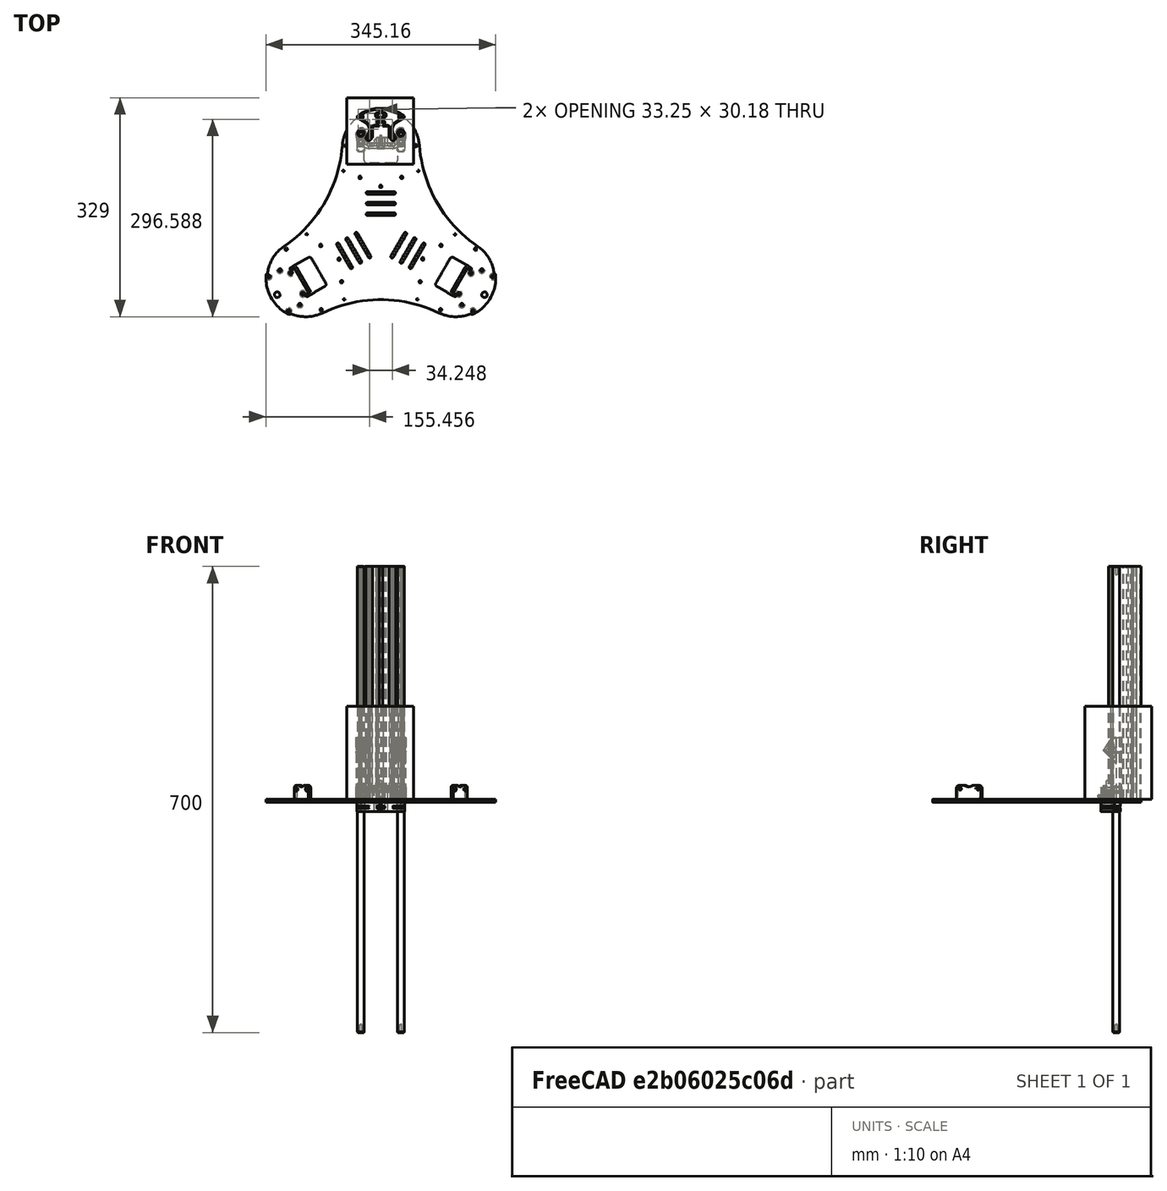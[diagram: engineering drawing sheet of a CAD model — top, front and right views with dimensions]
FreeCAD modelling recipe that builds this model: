
FCSTD DOCUMENT  (FreeCAD 0.18R16146 (Git))
Label: Vertical-Slider_w_FlyingExtruder
License: All rights reserved
LicenseURL: http://en.wikipedia.org/wiki/All_rights_reserved
objects: Part::FeaturePython×10, Part::Feature×9, Sketcher::SketchObject×6, App::Part×5, Part::Compound×3, PartDesign::Plane×3, PartDesign::Body×3, Spreadsheet::Sheet×2, PartDesign::Pocket×2, PartDesign::Hole×2, PartDesign::Revolution×1, Part::Box×1, App::DocumentObjectGroup×1, PartDesign::Point×1, PartDesign::AdditiveLoft×1, Part::Mirroring×1, PartDesign::FeatureBase×1, Part::MultiFuse×1
note: 51 computed .brp shape members not serialized (recipe doc carries the construction recipe); baked Part::Feature solids carry a one-line shape summary decoded from their .brp

FEATURE [Part::Feature] K8800_BAP
  Placement = pos=(0,-153,-2) rot=(0,0,1;0rad)
  shape: bbox 351.2 x 331.3 x 25.02 mm, 225 faces (baked)
FEATURE [Part::Feature] K8800_RD10  label="K8800_RodLeft"
  Placement = pos=(-30,0,0) rot=(0,0,1;0rad)
  shape: bbox 10 x 10 x 700 mm, 9 faces (baked)
FEATURE [Part::Feature] K8800_RD011  label="K8800_RodRight"
  Placement = pos=(30,0,0) rot=(0,0,1;0rad)
  shape: bbox 10 x 10 x 700 mm, 9 faces (baked)
FEATURE [Part::Feature] K8800_RI
  shape: bbox 70.64 x 62.27 x 700 mm, 164 faces (baked)
FEATURE [Part::Feature] K8800_VS
  Placement = pos=(0,0,0) rot=(0,0,1;1.5708rad)
  shape: bbox 72.01 x 24.93 x 46.6 mm, 535 faces (baked)
FEATURE [Part::Feature] K8800_LB10  label="K8800_LB10-L"
  Placement = pos=(-30,0,0) rot=(0,0,1;0rad)
  shape: bbox 12 x 12 x 36 mm, 16 faces (baked)
FEATURE [Part::Feature] K8800_LB10001  label="K8800_LB10-R"
  Placement = pos=(30,0,0) rot=(0,0,1;0rad)
  shape: bbox 12 x 12 x 36 mm, 16 faces (baked)
FEATURE [Spreadsheet::Sheet] Spreadsheet  label="Schrauben"
  cells = A1(M5RadiusBore)==2.5mm; B1=M5RadiusBore; C1=Radius der Bohrungen für M5-Schrauben; A2(M5HexNutWidth)==8mm; B2=M5HexNutWidth; C2=Schlüsselweite der M5-Muttern; A3(M5HexNutHeight)==4mm; B3=M5HexNutHeight; C3=Höhe der M5-Muttern; A4(M5HexHeadRadius)==4.7mm; B4=M5HexHeadRadius; C4=Radius des Schraubenkopfes; A5(M5HexHeadHeight)==5.1mm; B5=M5HexHeadHeight; C5=Höhe des Schraubenkopfes; A6(M5InsertHeight)==6mm; B6=M5InsertHeight; C6=Höhe des Insert; A7(M5InserWidth)==6.3mm; B7=M5InserWidth; C7=Durchmesser (Taille) des Insert; A8(MCThreadLength)==8.25mm; B8=MCThreadLength; C8=Gewindelänge der Magnetic Cups; A9(MCHeadHeight)==4.8mm; B9=MCHeadHeight; C9=Kopfhöhe der Magentic Cups; A10(MCHeadRadius)==8.5mm / 2; B10=MCHeadRadius; C10=Radius des Magnetic Cups
FEATURE [Spreadsheet::Sheet] Spreadsheet001  label="Global"
  cells = A1===========; B1=3D Druckparameter; C1===================================; A2(NozzleSize)==0.6mm; B2=NozzleSize; C2=Düsendurchmesser; A3(ExtMult)=0.9; B3=ExtMult; C3=Extrusion Multiplier; A4(NozzleWidth)==NozzleSize * ExtMult; B4=NozzeWidth; C4=Extrusion width; A5(numPerimeter)=3; B5=numPerimeter; C5=Anzahl der Perimeter; A6(Flesh)==2 * NozzleWidth; B6=Flesh; C6=Zusätzlicher Material; A7===========; B7=Bronzelager; C7===================================; A8(bearingID)==10mm; B8=bearingID; C8=Innendurchmesser Lager; A9(bearingOD)==13mm; B9=bearingOD; C9=Außendurchmesser Lager; A10(bearingLen)==20mm; B10=bearingLen; C10=Länge des Lagers; A11===========; B11=Mechanik Lager; C11===================================; A12(distRods)==60mm; B12=distRods; C12=Abstand der Wellen; A13(diaRods)==10mm; B13=diaRods; C13=Durchmesser der Wellen; A14(clearanceRods)==NozzleWidth / 2; B14=clearanceRods; C14=Sicherheitsabstand für diaRods; A15===========; B15=Laufbuchse; C15===================================; A16(bushingShrink)==NozzleWidth / 2; B16=bushingShrink; C16=radiale Schrumpfung für Laufbuchsen-Pressung; A17(bushingID)==bearingOD; B17=bushingID; C17=Innendurchmesser Laufbuchse; A18(bushingID3D)==bushingID - 2 * bushingShrink; B18=bushingID3D; C18=zu druckender Innendurchmesser Laufbuchse; A19(bushingOD3D)==bushingID3D + numPerimeter * NozzleWidth * 2; B19=bushingOD3D; C19=zu druckender Außendurchmesser Laufbuchse; A20(bushingIR3D)==bushingID3D / 2; B20=bushingIR3D; C20=effektiver innerer Radius der Laufbuchse; A21(bushingOR3D)==bushingOD3D / 2; B21=bushingOR3D; C21=effektiver äußerer Radius der Laufbuchse; A22(bushingWallTickness)==numPerimeter * NozzleWidth; B22=bushingWallTickness; C22=Wanddicke Laufbuchse; A23(bushingLength)==90mm; B23=bushingLength; C23=Gesamtlänge der Linearführung; A24(bushingRotArc)==300°; B24=bushingRotArc; C24=Rotationswinkel für Extrusion; A25===========; B25=Vertical Slider; C25===================================; A32===========; C32===================================; A33===========; C33===================================; A34===========; C34===================================; A35===========; C35===================================; A36===========; C36===================================; A37===========; C37===================================
FEATURE [Part::Feature] K8800_MC  label="K8800_MC-L"
  Placement = pos=(-30,-18,-3.1e-15) rot=(1,0,0;1.5708rad)
  shape: bbox 8.5 x 12.91 x 8.5 mm, 20 faces (baked)
FEATURE [Part::Feature] K8800_MC001  label="K8800_MC-R"
  Placement = pos=(30,-18,-3.1e-15) rot=(1,0,0;1.5708rad)
  shape: bbox 8.5 x 12.91 x 8.5 mm, 20 faces (baked)
FEATURE [Sketcher::SketchObject] Sketch
  MapMode = 5
  Placement = pos=(0,0,0) rot=(1,0,0;1.5708rad)
  Support = -> [XZ_Plane003]
  expr: Constraints[12] = <<Global>>.bushingWallTickness
  expr: Constraints[11] = <<Global>>.bushingWallTickness
  sketch-geometry (13):
    g0: LineSegment [constr] StartX=0 StartY=50 StartZ=0 EndX=0 EndY=-50 EndZ=0
    g1: LineSegment StartX=-6.23 StartY=48.24 StartZ=0 EndX=-6.23 EndY=27.16 EndZ=0
    g2: LineSegment StartX=-7.85 StartY=48.24 StartZ=0 EndX=-7.85 EndY=27.16 EndZ=0
    g3: LineSegment StartX=-5.54 StartY=25 StartZ=0 EndX=-5.54 EndY=-25 EndZ=0
    g4: LineSegment StartX=-7.16 StartY=25 StartZ=0 EndX=-7.16 EndY=-25 EndZ=0
    g5: LineSegment StartX=-7.85 StartY=-27.16 StartZ=0 EndX=-7.85 EndY=-48.24 EndZ=0
    g6: LineSegment StartX=-6.23 StartY=-27.16 StartZ=0 EndX=-6.23 EndY=-48.24 EndZ=0
    g7: LineSegment StartX=-7.85 StartY=-48.24 StartZ=0 EndX=-6.23 EndY=-48.24 EndZ=0
    g8: LineSegment StartX=-7.85 StartY=48.24 StartZ=0 EndX=-6.23 EndY=48.24 EndZ=0
    g9: LineSegment StartX=-7.85 StartY=27.16 StartZ=0 EndX=-7.16 EndY=25 EndZ=0
    g10: LineSegment StartX=-6.23 StartY=27.16 StartZ=0 EndX=-5.54 EndY=25 EndZ=0
    g11: LineSegment StartX=-7.16 StartY=-25 StartZ=0 EndX=-7.85 EndY=-27.16 EndZ=0
    g12: LineSegment StartX=-5.54 StartY=-25 StartZ=0 EndX=-6.23 EndY=-27.16 EndZ=0
  constraints (39):
    c: Vertical(g0)
    c: DistanceY(g0,g0) = 100
    c: Symmetric(g0,g0,g-1)
    c: Vertical(g1)
    c: Vertical(g2)
    c: Vertical(g3)
    c: Vertical(g4)
    c: Vertical(g5)
    c: Vertical(g6)
    c: Horizontal(g7)
    c: Perpendicular(g8,g0)
    c: DistanceX(g8,g8) = 1.62
    c: DistanceX(g7,g7) = 1.62
    c: Coincident(g7,g6)
    c: Coincident(g7,g5)
    c: Coincident(g2,g8)
    c: Coincident(g1,g8)
    c: DistanceX(g4,g3) = 1.62
    c: DistanceY(g2,g2) = 21.08  'upperBushingLeft'
    c: DistanceY(g1,g1) = 21.08  'upperBushingRight'
    c: DistanceY(g5,g5) = 21.08  'lowerBushingLeft'
    c: DistanceY(g6,g6) = 21.08  'lowerBushingRight'
    c: DistanceY(g4,g4) = 50
    c: Equal(g4,g3)
    c: DistanceY(g3,g-1) = 25
    c: DistanceY(g4,g-1) = 25
    c: DistanceX(g1,g0) = 6.23
    c: DistanceX(g6,g-1) = 6.23
    c: DistanceY(g3,g1) = 2.16
    c: Coincident(g1,g10)
    c: Coincident(g10,g3)
    c: Coincident(g9,g2)
    c: Coincident(g9,g4)
    c: DistanceY(g12,g12) = 2.16
    c: Coincident(g12,g3)
    c: Coincident(g11,g4)
    c: DistanceX(g3,g-1) = 5.54
    c: Coincident(g12,g6)
    c: Coincident(g11,g5)
FEATURE [PartDesign::Revolution] Revolution
  Angle = 300
  Axis = (0,-2e-16,1)
  Base = (0,0,0)
  Placement = pos=(0,0,0) rot=(1,0,0;1.5708rad)
  Profile = -> Sketch
  ReferenceAxis = -> Sketch [V_Axis]
  expr: Angle = <<Global>>.bushingRotArc
FEATURE [App::Part] Part003  label="Velleman CAD"
  Group = -> [K8800_VS,K8800_LB10,K8800_LB10001,K8800_MC,K8800_MC001]
  Origin = -> Origin005
FEATURE [App::Part] Part  label="K8800-VerticalSlider"
  Group = -> [Part003]
  Origin = -> Origin
FEATURE [Part::Box] Box  label="Cube"
  AttacherType = Attacher::AttachEngine3D
  Height = 140
  Length = 100
  Placement = pos=(-51,-47,0) rot=(0,0,1;0rad)
  Width = 100
FEATURE [App::Part] Part004  label="Velleman CAD001"
  Origin = -> Origin006
FEATURE [Part::Compound] Compound
  Links = -> [K8800_RI,K8800_RD011,K8800_RD10]
FEATURE [Part::FeaturePython] Slice  # WARN: FeaturePython — macro-defined, semantics opaque (R4)
  Base = -> Compound
  Mode = 1
  Tolerance = 0
  Tools = -> [Box]
  Visibility1 = false
FEATURE [Part::FeaturePython] Slice_child0  label="Slice.0"  # WARN: FeaturePython — macro-defined, semantics opaque (R4)
  Base = -> Slice
  FilterType = 1
  Invert = false
  OverrideMaxVal = 0
  Visibility1 = false
  WindowFrom = 80
  WindowTo = 100
  items = 0
FEATURE [Part::FeaturePython] Slice_child1  label="Slice.1"  # WARN: FeaturePython — macro-defined, semantics opaque (R4)
  Base = -> Slice
  FilterType = 1
  Invert = false
  OverrideMaxVal = 0
  Visibility1 = true
  WindowFrom = 80
  WindowTo = 100
  items = 1
FEATURE [Part::FeaturePython] Slice_child2  label="Slice.2"  # WARN: FeaturePython — macro-defined, semantics opaque (R4)
  Base = -> Slice
  FilterType = 1
  Invert = false
  OverrideMaxVal = 0
  Visibility1 = false
  WindowFrom = 80
  WindowTo = 100
  items = 2
FEATURE [Part::FeaturePython] Slice_child3  label="Slice.3"  # WARN: FeaturePython — macro-defined, semantics opaque (R4)
  Base = -> Slice
  FilterType = 1
  Invert = false
  OverrideMaxVal = 0
  Visibility1 = false
  WindowFrom = 80
  WindowTo = 100
  items = 3
FEATURE [Part::FeaturePython] Slice_child4  label="Slice.4"  # WARN: FeaturePython — macro-defined, semantics opaque (R4)
  Base = -> Slice
  FilterType = 1
  Invert = false
  OverrideMaxVal = 0
  Visibility1 = true
  WindowFrom = 80
  WindowTo = 100
  items = 4
FEATURE [Part::FeaturePython] Slice_child5  label="Slice.5"  # WARN: FeaturePython — macro-defined, semantics opaque (R4)
  Base = -> Slice
  FilterType = 1
  Invert = false
  OverrideMaxVal = 0
  Visibility1 = false
  WindowFrom = 80
  WindowTo = 100
  items = 5
FEATURE [Part::FeaturePython] Slice_child6  label="Slice.6"  # WARN: FeaturePython — macro-defined, semantics opaque (R4)
  Base = -> Slice
  FilterType = 1
  Invert = false
  OverrideMaxVal = 0
  Visibility1 = false
  WindowFrom = 80
  WindowTo = 100
  items = 6
FEATURE [Part::FeaturePython] Slice_child7  label="Slice.7"  # WARN: FeaturePython — macro-defined, semantics opaque (R4)
  Base = -> Slice
  FilterType = 1
  Invert = false
  OverrideMaxVal = 0
  Visibility1 = true
  WindowFrom = 80
  WindowTo = 100
  items = 7
FEATURE [Part::FeaturePython] Slice_child8  label="Slice.8"  # WARN: FeaturePython — macro-defined, semantics opaque (R4)
  Base = -> Slice
  FilterType = 1
  Invert = false
  OverrideMaxVal = 0
  Visibility1 = false
  WindowFrom = 80
  WindowTo = 100
  items = 8
FEATURE [App::DocumentObjectGroup] GrExplode_Slice  label="Exploded Slice"
  Group = -> [Slice_child0,Slice_child1,Slice_child2,Slice_child3,Slice_child4,Slice_child5,Slice_child6,Slice_child7,Slice_child8]
FEATURE [App::Part] Part001  label="VerticalRods"
  Group = -> [Part004,Box,K8800_RI,K8800_RD011,K8800_RD10,Compound,Slice,Slice_child1,Slice_child7,Slice_child6,Slice_child0,Slice_child2,Slice_child3,Slice_child5,Slice_child4,Slice_child8,GrExplode_Slice]
  Origin = -> Origin001
  Placement = pos=(0,0,-20) rot=(0,0,1;0rad)
FEATURE [Sketcher::SketchObject] Sketch004
  AttachmentOffset = pos=(0,1,7) rot=(0,0,1;0rad)
  MapMode = 5
  Placement = pos=(0,-7,1) rot=(1,0,0;1.5708rad)
  Support = -> [XZ_Plane022]
  sketch-geometry (5):
    g0: Ellipse CenterX=-30 CenterY=66 CenterZ=0 NormalX=0 NormalY=0 NormalZ=1 MajorRadius=17 MinorRadius=7 AngleXU=-1.5708
    g1: LineSegment [constr] StartX=-30 StartY=49 StartZ=0 EndX=-30 EndY=83 EndZ=0
    g2: LineSegment [constr] StartX=-23 StartY=66 StartZ=0 EndX=-37 EndY=66 EndZ=0
    g3: GeomPoint X=-30 Y=50.5081 Z=0
    g4: GeomPoint X=-30 Y=81.4919 Z=0
  constraints (6):
    c: InternalAlignment(g1-g4 -> g0) x4
    c: DistanceX(g0,g-1) = 30
    c: DistanceX(g2,g2) = 14
    c: DistanceY(g1,g1) = 34
    c: DistanceY(g-1,g2) = 66
    c: Parallel(g1,g-2)
FEATURE [PartDesign::Point] DatumPoint
  AttacherType = Attacher::AttachEnginePoint
  MapMode = 37
  Placement = pos=(-30,-7,67.0566) rot=(0,0,1;0rad)
  Support = -> [Sketch004]
FEATURE [Sketcher::SketchObject] Sketch005
  ExternalGeometry = -> [DatumPoint]
  MapMode = 5
  Placement = pos=(0,0,0) rot=(1,0,0;1.5708rad)
  Support = -> [XZ_Plane022]
  expr: Constraints[7] = Global.distRods / 2
  expr: Constraints[6] = <<Global>>.bushingOD3D - 1.5mm
  sketch-geometry (5):
    g0: LineSegment StartX=-37.1 StartY=83.0566 StartZ=0 EndX=-22.9 EndY=83.0566 EndZ=0
    g1: LineSegment StartX=-22.9 StartY=83.0566 StartZ=0 EndX=-22.9 EndY=43.0566 EndZ=0
    g2: LineSegment StartX=-22.9 StartY=43.0566 StartZ=0 EndX=-37.1 EndY=43.0566 EndZ=0
    g3: LineSegment StartX=-37.1 StartY=43.0566 StartZ=0 EndX=-37.1 EndY=83.0566 EndZ=0
    g4: LineSegment [constr] StartX=-30 StartY=83.0566 StartZ=0 EndX=-30 EndY=32.8566 EndZ=0
  constraints (14):
    c: Coincident(g0,g1)
    c: Coincident(g1,g2)
    c: Coincident(g2,g3)
    c: Coincident(g3,g0)
    c: Horizontal(g2)
    c: Vertical(g1)
    c: DistanceX(g0,g0) = 14.2
    c: DistanceX(g4,g-1) = 30
    c: Symmetric(g1,g2,g4)
    c: Symmetric(g0,g0,g4)
    c: Distance(g4) = 50.2
    c: DistanceY(g-3,g4) = 16
    c: DistanceY(g0,g4) = 0
    c: Distance(g0,g1) = 40
FEATURE [PartDesign::Plane] DatumPlane
  Length = 59.9179
  MapMode = 1
  Placement = pos=(-30,-7,67.0566) rot=(1,0,0;-0.785398rad)
  ResizeMode = 0
  Support = -> [DatumPoint]
  Width = 100.026
FEATURE [Sketcher::SketchObject] Sketch006
  AttachmentOffset = pos=(0,6,-11) rot=(0,0,1;0rad)
  MapMode = 5
  Placement = pos=(-30,-10.5355,55.0358) rot=(-1,0,0;0.785398rad)
  Support = -> [DatumPlane]
  sketch-geometry (1):
    g0: Circle CenterX=0 CenterY=-6.95 CenterZ=0 NormalX=0 NormalY=0 NormalZ=1 AngleXU=0 Radius=5.5
  constraints (3):
    c: Radius(g0) = 5.5
    c: DistanceY(g0,g-1) = 6.95
    c: DistanceX(g-1,g0) = 0
FEATURE [PartDesign::AdditiveLoft] AdditiveLoft
  Closed = false
  Placement = pos=(0,0,0) rot=(1,0,0;1.5708rad)
  Profile = -> Sketch005
  Ruled = true
  Sections = -> [Sketch004,Sketch006]
FEATURE [PartDesign::Plane] DatumPlane001
  AttachmentOffset = pos=(-20,-80,-7.85) rot=(0,0,1;0rad)
  Length = 40
  MapMode = 3
  Placement = pos=(-50,0.85,-12.9434) rot=(1,0,0;1.5708rad)
  ResizeMode = 1
  Support = -> [DatumPoint]
  Width = 100
  expr: AttachmentOffset.Base.z = -Global.bushingOR3D
FEATURE [PartDesign::Plane] DatumPlane002
  AttachmentOffset = pos=(0,0,-1) rot=(0,0,1;0rad)
  Length = 37.5887
  MapMode = 45
  Placement = pos=(0.244953,-0.141423,2.7e-15) rot=(0.774597,0.447214,0.447214;1.82348rad)
  ResizeMode = 0
  Support = -> [Revolution]
  Width = 106.748
FEATURE [PartDesign::Body] Body  label="bearing (links)"
  Group = -> [Sketch,Revolution,DatumPlane002]
  Origin = -> Origin003
  Placement = pos=(-30,0,45) rot=(0,0,1;0rad)
  Tip = -> Revolution
FEATURE [Part::Mirroring] Part__Mirroring  label="bearing (rechts)"
  Base = (0,0,0)
  Normal = (1,0,0)
  Source = -> Body
FEATURE [Sketcher::SketchObject] Sketch007  label="ReibAhle#001"
  MapMode = 5
  Support = -> [XY_Plane022]
  expr: Constraints[2] = Global.bushingIR3D
  expr: Constraints[0] = Global.distRods / 2
  sketch-geometry (1):
    g0: Circle [constr] CenterX=-30 CenterY=0 CenterZ=0 NormalX=0 NormalY=0 NormalZ=1 AngleXU=0 Radius=6.23
  constraints (3):
    c: DistanceX(g0,g-1) = 30
    c: DistanceY(g-1,g0) = 0
    c: Radius(g0) = 6.23
FEATURE [Sketcher::SketchObject] Sketch008  label="ReibAhle#002"
  MapMode = 5
  Support = -> [XY_Plane022]
  expr: Constraints[2] = Global.diaRods / 2 + Global.NozzleWidth
  expr: Constraints[0] = Global.distRods / 2
  sketch-geometry (1):
    g0: Circle [constr] CenterX=-30 CenterY=0 CenterZ=0 NormalX=0 NormalY=0 NormalZ=1 AngleXU=0 Radius=5.54
  constraints (3):
    c: DistanceX(g0,g-1) = 30
    c: DistanceY(g-1,g0) = 0
    c: Radius(g0) = 5.54
FEATURE [PartDesign::Pocket] Pocket
  BaseFeature = -> AdditiveLoft
  Length = 21.08
  Length2 = 100
  Placement = pos=(0,0,0) rot=(1,0,0;1.5708rad)
  Profile = -> AdditiveLoft [Face2]
  Type = 0
  expr: Length = Global.bearingLen + 2 * Global.NozzleWidth
FEATURE [PartDesign::Pocket] Pocket001
  BaseFeature = -> Pocket
  Length = 50
  Length2 = 100
  Placement = pos=(0,0,0) rot=(1,0,0;1.5708rad)
  Profile = -> Pocket [Face8]
  Type = 0
  expr: Length = Global.bushingLength - 2 * Global.bearingLen
FEATURE [PartDesign::Hole] Hole
  BaseFeature = -> Pocket001
  Depth = 25
  DepthType = 0
  Diameter = 5
  DrillPoint = 0
  DrillPointAngle = 118
  HoleCutCountersinkAngle = 90
  HoleCutDepth = 9
  HoleCutDiameter = 6.3
  HoleCutType = 1
  ModelActualThread = false
  Placement = pos=(0,0,0) rot=(1,0,0;1.5708rad)
  Profile = -> Pocket001 [Face15]
  Tapered = false
  TaperedAngle = 90
  ThreadAngle = 0
  ThreadClass = 0
  ThreadCutOffInner = 0
  ThreadCutOffOuter = 0
  ThreadDirection = 0
  ThreadFit = 0
  ThreadPitch = 0
  ThreadSize = 0
  ThreadType = 0
  Threaded = false
  expr: HoleCutDepth = 3mm + Schrauben.M5InsertHeight
  expr: HoleCutDiameter = Schrauben.M5InserWidth
  expr: Diameter = 2 * Schrauben.M5RadiusBore
FEATURE [PartDesign::Hole] Hole001
  BaseFeature = -> Hole
  Depth = 2.5
  DepthType = 0
  Diameter = 9.4
  DrillPoint = 0
  DrillPointAngle = 118
  HoleCutCountersinkAngle = 90
  HoleCutDepth = 0
  HoleCutDiameter = 0
  HoleCutType = 0
  ModelActualThread = false
  Placement = pos=(0,0,0) rot=(1,0,0;1.5708rad)
  Profile = -> Hole [Face15]
  Tapered = false
  TaperedAngle = 90
  ThreadAngle = 0
  ThreadClass = 0
  ThreadCutOffInner = 0
  ThreadCutOffOuter = 0
  ThreadDirection = 0
  ThreadFit = 0
  ThreadPitch = 0
  ThreadSize = 0
  ThreadType = 0
  Threaded = false
  expr: Depth = 2.5mm
  expr: Diameter = Schrauben.M5HexHeadRadius * 2
FEATURE [PartDesign::Body] Body017  label="Gelenkkopf (links)"
  Group = -> [Sketch004,Sketch005,DatumPoint,DatumPlane,Sketch006,AdditiveLoft,DatumPlane001,Sketch007,Sketch008,Pocket,Pocket001,Hole,Hole001]
  Origin = -> Origin022
  Placement = pos=(0,0,10) rot=(0,0,1;0rad)
  Tip = -> Hole001
FEATURE [PartDesign::FeatureBase] Clone
  BaseFeature = -> Body017
  Placement = pos=(0,0,10) rot=(0,0,1;0rad)
FEATURE [PartDesign::Body] Body019  label="Gelenkkopf (rechts)"
  Group = -> [Clone]
  Origin = -> Origin024
  Placement = pos=(60,0,0) rot=(0,0,1;0rad)
  Tip = -> Clone
  expr: Placement.Base.x = Global.distRods
FEATURE [App::Part] Part002  label="Vertex Delta K8800"
  Group = -> [Part,K8800_BAP,Part001,Body,Body017,Body019,Part__Mirroring]
  Origin = -> Origin002
FEATURE [Part::Compound] Compound001  label="Vertical Slider (left)"
  Links = -> [Body017,Body]
FEATURE [Part::Compound] Compound002  label="Vertical Slider (right)"
  Links = -> [Part__Mirroring,Body019]
FEATURE [Part::MultiFuse] Fusion
  Shapes = -> [Compound001]
